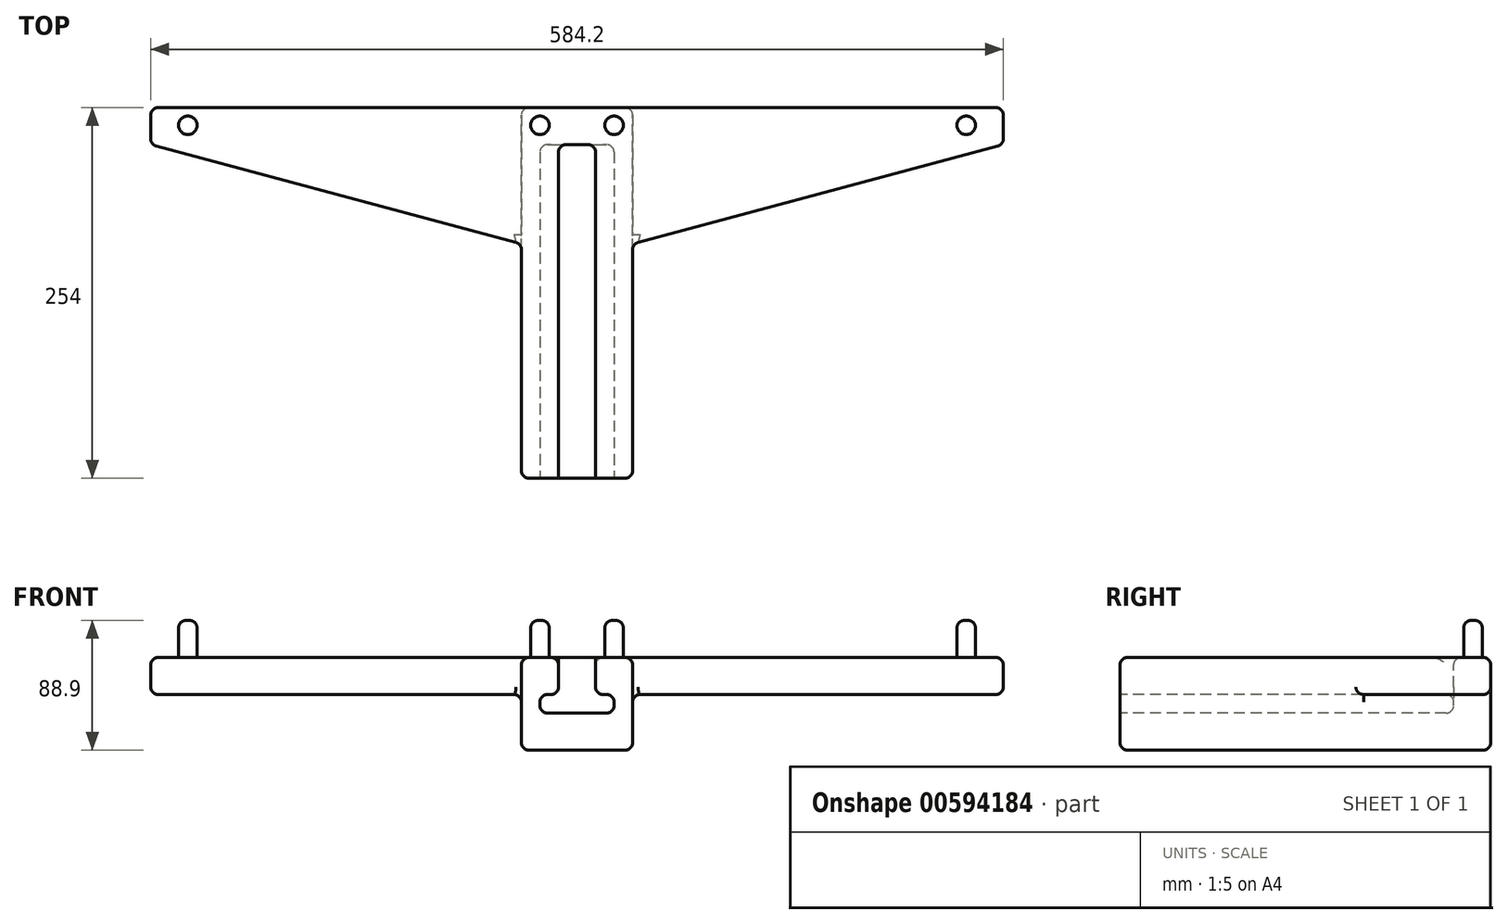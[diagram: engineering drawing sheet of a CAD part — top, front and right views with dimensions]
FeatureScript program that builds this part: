
annotation { "Feature Type Name" : "Feature", "Feature Type Description" : "" }
export const myFeature = defineFeature(function(context is Context, id is Id, definition is map)
    precondition{}
    {
        {
            var Q0;
            Q0=qCreatedBy(makeId("Front.planeOp"),FACE);
            var sketch = newSketch(context, id + "F0", { "sketchPlane" : qUnion([Q0])});
            skLineSegment(sketch, "E0.bottom", {"start": v(-38.93, 38.6) * mm, "end": v(37.27, 38.6) * mm});
            skLineSegment(sketch, "E0.top", {"start": v(-38.93, -24.9) * mm, "end": v(37.27, -24.9) * mm});
            skLineSegment(sketch, "E0.left", {"start": v(-38.93, 38.6) * mm, "end": v(-38.93, -24.9) * mm});
            skLineSegment(sketch, "E0.right", {"start": v(37.27, 38.6) * mm, "end": v(37.27, -24.9) * mm});
            skSolve(sketch);
        }
        {
            var Q0;
            Q0=makeQuery(id+"F0.imprint","IMPRINT",FACE,{"disambiguationData":[TD([[makeQuery(id+"F0.imprint","IMPRINT",EDGE,{"derivedFrom":sQuery(id+"F0.wireOp",EDGE,"E0.bottom")}),-1.0]])]});
            extrude(context, id + "F1", {"entities" : qUnion([Q0]), "endBound" : BoundingType.SYMMETRIC, "depth" : 254 * mm, "offsetDistance" : 25.4 * mm});
        }
        {
            var Q0;
            Q0=makeQuery(id+"F1.opExtrude","CAP_FACE",FACE,{"disambiguationData":[OSD([sQuery(id+"F0.wireOp",EDGE,"E0.bottom"),sQuery(id+"F0.wireOp",EDGE,"E0.top"),sQuery(id+"F0.wireOp",EDGE,"E0.left"),sQuery(id+"F0.wireOp",EDGE,"E0.right")])],"isStart":false});
            var sketch = newSketch(context, id + "F2", { "sketchPlane" : qUnion([Q0])});
            skLineSegment(sketch, "E1", {"start": v(-38.93, 38.6) * mm, "end": v(-13.53, 38.6) * mm, "construction": true});
            skLineSegment(sketch, "E2", {"start": v(37.27, 38.6) * mm, "end": v(11.87, 38.6) * mm, "construction": true});
            skLineSegment(sketch, "E3", {"start": v(-13.53, 38.6) * mm, "end": v(-13.53, 13.2) * mm});
            skLineSegment(sketch, "E4", {"start": v(-13.53, 13.2) * mm, "end": v(-26.23, 13.2) * mm});
            skLineSegment(sketch, "E5", {"start": v(-26.23, 13.2) * mm, "end": v(-26.23, 0.5) * mm});
            skLineSegment(sketch, "E6", {"start": v(-26.23, 0.5) * mm, "end": v(24.57, 0.5) * mm});
            skLineSegment(sketch, "E7", {"start": v(24.57, 0.5) * mm, "end": v(24.57, 13.2) * mm});
            skLineSegment(sketch, "E8", {"start": v(24.57, 13.2) * mm, "end": v(11.87, 13.2) * mm});
            skLineSegment(sketch, "E9", {"start": v(11.87, 13.2) * mm, "end": v(11.87, 38.6) * mm});
            skLineSegment(sketch, "E10", {"start": v(-13.53, 38.6) * mm, "end": v(11.87, 38.6) * mm});
            skSolve(sketch);
        }
        {
            var Q0;
            Q0 = qSketchRegion(id + "F2", true);
            extrude(context, id + "F3", {"entities" : qUnion([Q0]), "operationType" : NewBodyOperationType.REMOVE, "oppositeDirection" : true, "depth" : 228.6 * mm, "offsetDistance" : 25.4 * mm});
        }
        {
            var Q0;
            Q0=makeQuery(id+"F1.opExtrude","SWEPT_FACE",FACE,{"disambiguationData":[OSD([sQuery(id+"F0.wireOp",EDGE,"E0.bottom")])]});
            var sketch = newSketch(context, id + "F4", { "sketchPlane" : qUnion([Q0])});
            skLineSegment(sketch, "E11", {"start": v(-38.93, 114.88) * mm, "end": v(-26.23, 114.88) * mm, "construction": true});
            skLineSegment(sketch, "E12", {"start": v(37.27, 114.88) * mm, "end": v(24.57, 114.88) * mm, "construction": true});
            skCircle(sketch, "E13", {"center": v(-26.23, 114.88) * mm, "radius": 6.35 * mm});
            skCircle(sketch, "E14", {"center": v(24.57, 114.88) * mm, "radius": 6.35 * mm});
            skSolve(sketch);
        }
        {
            var Q0;
            Q0 = qSketchRegion(id + "F4", true);
            extrude(context, id + "F5", {"entities" : qUnion([Q0]), "operationType" : NewBodyOperationType.ADD, "depth" : 25.4 * mm, "offsetDistance" : 25.4 * mm});
        }
        {
            var Q0;
            Q0=makeQuery(id+"F1.opExtrude","SWEPT_FACE",FACE,{"disambiguationData":[OSD([sQuery(id+"F0.wireOp",EDGE,"E0.right")])]});
            var sketch = newSketch(context, id + "F6", { "sketchPlane" : qUnion([Q0])});
            skLineSegment(sketch, "E15.bottom", {"start": v(127, 38.6) * mm, "end": v(25.4, 38.6) * mm});
            skLineSegment(sketch, "E15.top", {"start": v(127, 13.2) * mm, "end": v(25.4, 13.2) * mm});
            skLineSegment(sketch, "E15.left", {"start": v(127, 38.6) * mm, "end": v(127, 13.2) * mm});
            skLineSegment(sketch, "E15.right", {"start": v(25.4, 38.6) * mm, "end": v(25.4, 13.2) * mm});
            skSolve(sketch);
        }
        {
            var Q0;
            Q0 = qSketchRegion(id + "F6", true);
            extrude(context, id + "F7", {"entities" : qUnion([Q0]), "operationType" : NewBodyOperationType.ADD, "depth" : 254 * mm, "offsetDistance" : 25.4 * mm});
        }
        {
            var Q0;
            Q0=makeQuery(id+"F7.opExtrude","CAP_EDGE",EDGE,{"disambiguationData":[OSD([sQuery(id+"F6.wireOp",EDGE,"E15.right")])],"isStart":false});
            chamfer(context, id + "F8", {"entities" : qUnion([Q0]), "chamferType" : ChamferType.OFFSET_ANGLE, "width" : 76.2 * mm, "oppositeDirection" : false, "angle" : 75 * degree, "tangentPropagation" : true});
        }
        {
            var Q0;
            Q0=makeQuery(id+"F1.opExtrude","SWEPT_FACE",FACE,{"disambiguationData":[OSD([sQuery(id+"F0.wireOp",EDGE,"E0.left")])]});
            var sketch = newSketch(context, id + "F9", { "sketchPlane" : qUnion([Q0])});
            skLineSegment(sketch, "E16.bottom", {"start": v(-127, 38.6) * mm, "end": v(-25.4, 38.6) * mm});
            skLineSegment(sketch, "E16.top", {"start": v(-127, 13.2) * mm, "end": v(-25.4, 13.2) * mm});
            skLineSegment(sketch, "E16.left", {"start": v(-127, 38.6) * mm, "end": v(-127, 13.2) * mm});
            skLineSegment(sketch, "E16.right", {"start": v(-25.4, 38.6) * mm, "end": v(-25.4, 13.2) * mm});
            skSolve(sketch);
        }
        {
            var Q0;
            Q0=makeQuery(id+"F9.imprint","IMPRINT",FACE,{"disambiguationData":[TD([[makeQuery(id+"F9.imprint","IMPRINT",EDGE,{"derivedFrom":sQuery(id+"F9.wireOp",EDGE,"E16.bottom")}),1.0]])]});
            extrude(context, id + "F10", {"entities" : qUnion([Q0]), "operationType" : NewBodyOperationType.ADD, "depth" : 254 * mm, "offsetDistance" : 25.4 * mm});
        }
        {
            var Q0;
            Q0=makeQuery(id+"F10.opExtrude","CAP_EDGE",EDGE,{"disambiguationData":[OSD([sQuery(id+"F9.wireOp",EDGE,"E16.right")])],"isStart":false});
            chamfer(context, id + "F11", {"entities" : qUnion([Q0]), "chamferType" : ChamferType.OFFSET_ANGLE, "width" : 76.2 * mm, "oppositeDirection" : true, "angle" : 75 * degree, "tangentPropagation" : true});
        }
        {
            var Q0;
            Q0=makeQuery(id+"F7.opExtrude","SWEPT_EDGE",EDGE,{"disambiguationData":[OSD([sQuery(id+"F0.wireOp",EDGE,"E0.right"),sQuery(id+"F6.wireOp",EDGE,"E15.top"),sQuery(id+"F6.wireOp",EDGE,"E15.left")])]});
            var Q1;
            Q1=makeQuery(id+"F10.opExtrude","SWEPT_EDGE",EDGE,{"disambiguationData":[OSD([sQuery(id+"F0.wireOp",EDGE,"E0.left"),sQuery(id+"F9.wireOp",EDGE,"E16.top"),sQuery(id+"F9.wireOp",EDGE,"E16.left")])]});
            var Q2;
            Q2=makeQuery(id+"F1.opExtrude","CAP_EDGE",EDGE,{"disambiguationData":[OSD([sQuery(id+"F0.wireOp",EDGE,"E0.right")])],"isStart":true});
            var Q3;
            Q3=makeQuery(id+"F1.opExtrude","CAP_EDGE",EDGE,{"disambiguationData":[OSD([sQuery(id+"F0.wireOp",EDGE,"E0.left")])],"isStart":true});
            var Q4;
            Q4=makeQuery(id+"F1.opExtrude","SWEPT_EDGE",EDGE,{"disambiguationData":[OSD([sQuery(id+"F0.wireOp",EDGE,"E0.top"),sQuery(id+"F0.wireOp",EDGE,"E0.left")])]});
            var Q5;
            Q5=makeQuery(id+"F1.opExtrude","CAP_EDGE",EDGE,{"disambiguationData":[OSD([sQuery(id+"F0.wireOp",EDGE,"E0.top")])],"isStart":true});
            var Q6;
            Q6=makeQuery(id+"F1.opExtrude","SWEPT_EDGE",EDGE,{"disambiguationData":[OSD([sQuery(id+"F0.wireOp",EDGE,"E0.top"),sQuery(id+"F0.wireOp",EDGE,"E0.right")])]});
            var Q7;
            Q7=makeQuery(id+"F1.opExtrude","CAP_EDGE",EDGE,{"disambiguationData":[OSD([sQuery(id+"F0.wireOp",EDGE,"E0.top")])],"isStart":false});
            var Q8;
            Q8=makeQuery(id+"F1.opExtrude","SWEPT_EDGE",EDGE,{"disambiguationData":[OSD([sQuery(id+"F0.wireOp",EDGE,"E0.bottom"),sQuery(id+"F0.wireOp",EDGE,"E0.right")])]});
            var Q9;
            Q9=makeQuery(id+"F3.boolean.opBoolean","COPY",EDGE,{"derivedFrom":makeQuery(id+"F3.opExtrude","SWEPT_EDGE",EDGE,{"disambiguationData":[OSD([sQuery(id+"F0.wireOp",EDGE,"E0.bottom"),sQuery(id+"F2.wireOp",EDGE,"E3"),sQuery(id+"F2.wireOp",EDGE,"E10")])]})});
            var Q10;
            Q10=makeQuery(id+"F8.opChamfer","BLEND_EDGE",EDGE,{"blendedFrom":[makeQuery(id+"F7.opExtrude","CAP_EDGE",EDGE,{"disambiguationData":[OSD([sQuery(id+"F6.wireOp",EDGE,"E15.right")])],"isStart":false}),makeQuery(id+"F7.boolean.opBoolean","MERGE",FACE,{"derivedFrom":[makeQuery(id+"F1.opExtrude","SWEPT_FACE",FACE,{"disambiguationData":[OSD([sQuery(id+"F0.wireOp",EDGE,"E0.bottom")])]}),makeQuery(id+"F7.opExtrude","SWEPT_FACE",FACE,{"disambiguationData":[OSD([sQuery(id+"F6.wireOp",EDGE,"E15.bottom")])]})]})],"blendedInto":[makeQuery(id+"F7.boolean.opBoolean","MERGE",FACE,{"derivedFrom":[makeQuery(id+"F1.opExtrude","SWEPT_FACE",FACE,{"disambiguationData":[OSD([sQuery(id+"F0.wireOp",EDGE,"E0.bottom")])]}),makeQuery(id+"F7.opExtrude","SWEPT_FACE",FACE,{"disambiguationData":[OSD([sQuery(id+"F6.wireOp",EDGE,"E15.bottom")])]})]})]});
            var Q11;
            Q11=makeQuery(id+"F11.opChamfer","BLEND_EDGE",EDGE,{"blendedFrom":[makeQuery(id+"F10.opExtrude","CAP_EDGE",EDGE,{"disambiguationData":[OSD([sQuery(id+"F9.wireOp",EDGE,"E16.right")])],"isStart":false}),makeQuery(id+"F10.boolean.opBoolean","MERGE",FACE,{"derivedFrom":[makeQuery(id+"F7.boolean.opBoolean","MERGE",FACE,{"derivedFrom":[makeQuery(id+"F1.opExtrude","SWEPT_FACE",FACE,{"disambiguationData":[OSD([sQuery(id+"F0.wireOp",EDGE,"E0.bottom")])]}),makeQuery(id+"F7.opExtrude","SWEPT_FACE",FACE,{"disambiguationData":[OSD([sQuery(id+"F6.wireOp",EDGE,"E15.bottom")])]})]}),makeQuery(id+"F10.opExtrude","SWEPT_FACE",FACE,{"disambiguationData":[OSD([sQuery(id+"F9.wireOp",EDGE,"E16.bottom")])]})]})],"blendedInto":[makeQuery(id+"F10.boolean.opBoolean","MERGE",FACE,{"derivedFrom":[makeQuery(id+"F7.boolean.opBoolean","MERGE",FACE,{"derivedFrom":[makeQuery(id+"F1.opExtrude","SWEPT_FACE",FACE,{"disambiguationData":[OSD([sQuery(id+"F0.wireOp",EDGE,"E0.bottom")])]}),makeQuery(id+"F7.opExtrude","SWEPT_FACE",FACE,{"disambiguationData":[OSD([sQuery(id+"F6.wireOp",EDGE,"E15.bottom")])]})]}),makeQuery(id+"F10.opExtrude","SWEPT_FACE",FACE,{"disambiguationData":[OSD([sQuery(id+"F9.wireOp",EDGE,"E16.bottom")])]})]})]});
            var Q12;
            Q12=makeQuery(id+"F3.boolean.opBoolean","COPY",EDGE,{"derivedFrom":makeQuery(id+"F3.opExtrude","CAP_EDGE",EDGE,{"disambiguationData":[OSD([sQuery(id+"F2.wireOp",EDGE,"E9")])],"isStart":true})});
            var Q13;
            Q13=makeQuery(id+"F3.boolean.opBoolean","COPY",EDGE,{"derivedFrom":makeQuery(id+"F3.opExtrude","CAP_EDGE",EDGE,{"disambiguationData":[OSD([sQuery(id+"F2.wireOp",EDGE,"E3")])],"isStart":true})});
            var Q14;
            Q14=makeQuery(id+"F3.boolean.opBoolean","COPY",EDGE,{"derivedFrom":makeQuery(id+"F3.opExtrude","CAP_EDGE",EDGE,{"disambiguationData":[OSD([sQuery(id+"F2.wireOp",EDGE,"E6")])],"isStart":true})});
            var Q15;
            Q15=makeQuery(id+"F3.boolean.opBoolean","COPY",EDGE,{"derivedFrom":makeQuery(id+"F3.opExtrude","SWEPT_EDGE",EDGE,{"disambiguationData":[OSD([sQuery(id+"F2.wireOp",EDGE,"E6"),sQuery(id+"F2.wireOp",EDGE,"E7")])]})});
            var Q16;
            Q16=makeQuery(id+"F3.boolean.opBoolean","COPY",EDGE,{"derivedFrom":makeQuery(id+"F3.opExtrude","SWEPT_EDGE",EDGE,{"disambiguationData":[OSD([sQuery(id+"F2.wireOp",EDGE,"E8"),sQuery(id+"F2.wireOp",EDGE,"E9")])]})});
            var Q17;
            Q17=makeQuery(id+"F3.boolean.opBoolean","COPY",EDGE,{"derivedFrom":makeQuery(id+"F3.opExtrude","SWEPT_EDGE",EDGE,{"disambiguationData":[OSD([sQuery(id+"F2.wireOp",EDGE,"E3"),sQuery(id+"F2.wireOp",EDGE,"E4")])]})});
            var Q18;
            Q18=makeQuery(id+"F1.opExtrude","CAP_EDGE",EDGE,{"disambiguationData":[OSD([sQuery(id+"F0.wireOp",EDGE,"E0.right")])],"isStart":false});
            var Q19;
            Q19=makeQuery(id+"F3.boolean.opBoolean","COPY",EDGE,{"derivedFrom":makeQuery(id+"F3.opExtrude","SWEPT_EDGE",EDGE,{"disambiguationData":[OSD([sQuery(id+"F2.wireOp",EDGE,"E4"),sQuery(id+"F2.wireOp",EDGE,"E5")])]})});
            var Q20;
            Q20=makeQuery(id+"F3.boolean.opBoolean","COPY",EDGE,{"derivedFrom":makeQuery(id+"F3.opExtrude","SWEPT_EDGE",EDGE,{"disambiguationData":[OSD([sQuery(id+"F2.wireOp",EDGE,"E5"),sQuery(id+"F2.wireOp",EDGE,"E6")])]})});
            var Q21;
            Q21=makeQuery(id+"F3.boolean.opBoolean","COPY",EDGE,{"derivedFrom":makeQuery(id+"F3.opExtrude","CAP_EDGE",EDGE,{"disambiguationData":[OSD([sQuery(id+"F2.wireOp",EDGE,"E8")])],"isStart":true})});
            var Q22;
            Q22=makeQuery(id+"F1.opExtrude","SWEPT_FACE",FACE,{"disambiguationData":[OSD([sQuery(id+"F0.wireOp",EDGE,"E0.left")])]});
            var Q23;
            Q23=makeQuery(id+"F1.opExtrude","SWEPT_FACE",FACE,{"disambiguationData":[OSD([sQuery(id+"F0.wireOp",EDGE,"E0.right")])]});
            var Q24;
            Q24=makeQuery(id+"F3.boolean.opBoolean","COPY",EDGE,{"derivedFrom":makeQuery(id+"F3.opExtrude","SWEPT_EDGE",EDGE,{"disambiguationData":[OSD([sQuery(id+"F0.wireOp",EDGE,"E0.bottom"),sQuery(id+"F2.wireOp",EDGE,"E9"),sQuery(id+"F2.wireOp",EDGE,"E10")])]})});
            var Q25;
            {var subQ0=sQuery(id+"F0.wireOp",EDGE,"E0.bottom");var subQ1=sQuery(id+"F0.wireOp",EDGE,"E0.right");Q25=makeQuery(id+"F3.boolean.opBoolean","SPLIT",EDGE,{"disambiguationData":[TD([makeQuery(id+"F1.opExtrude","SWEPT_FACE",FACE,{"disambiguationData":[OSD([subQ1])]})])],"derivedFrom":makeQuery(id+"F1.opExtrude","CAP_EDGE",EDGE,{"disambiguationData":[OSD([subQ0])],"isStart":false})});}
            var Q26;
            {var subQ0=sQuery(id+"F0.wireOp",EDGE,"E0.bottom");var subQ1=sQuery(id+"F0.wireOp",EDGE,"E0.left");Q26=makeQuery(id+"F3.boolean.opBoolean","SPLIT",EDGE,{"disambiguationData":[TD([makeQuery(id+"F1.opExtrude","SWEPT_FACE",FACE,{"disambiguationData":[OSD([subQ1])]})])],"derivedFrom":makeQuery(id+"F1.opExtrude","CAP_EDGE",EDGE,{"disambiguationData":[OSD([subQ0])],"isStart":false})});}
            var Q27;
            Q27=makeQuery(id+"F10.boolean.opBoolean","MERGE",EDGE,{"derivedFrom":[makeQuery(id+"F7.boolean.opBoolean","MERGE",EDGE,{"derivedFrom":[makeQuery(id+"F1.opExtrude","CAP_EDGE",EDGE,{"disambiguationData":[OSD([sQuery(id+"F0.wireOp",EDGE,"E0.bottom")])],"isStart":true}),makeQuery(id+"F7.opExtrude","SWEPT_EDGE",EDGE,{"disambiguationData":[OSD([sQuery(id+"F6.wireOp",EDGE,"E15.bottom"),sQuery(id+"F6.wireOp",EDGE,"E15.left")])]})]}),makeQuery(id+"F10.opExtrude","SWEPT_EDGE",EDGE,{"disambiguationData":[OSD([sQuery(id+"F9.wireOp",EDGE,"E16.bottom"),sQuery(id+"F9.wireOp",EDGE,"E16.left")])]})]});
            var Q28;
            Q28=makeQuery(id+"F3.boolean.opBoolean","COPY",EDGE,{"derivedFrom":makeQuery(id+"F3.opExtrude","SWEPT_EDGE",EDGE,{"disambiguationData":[OSD([sQuery(id+"F2.wireOp",EDGE,"E7"),sQuery(id+"F2.wireOp",EDGE,"E8")])]})});
            var Q29;
            Q29=makeQuery(id+"F3.boolean.opBoolean","COPY",FACE,{"derivedFrom":makeQuery(id+"F3.opExtrude","CAP_FACE",FACE,{"disambiguationData":[OSD([sQuery(id+"F2.wireOp",EDGE,"E3"),sQuery(id+"F2.wireOp",EDGE,"E4"),sQuery(id+"F2.wireOp",EDGE,"E5"),sQuery(id+"F2.wireOp",EDGE,"E6"),sQuery(id+"F2.wireOp",EDGE,"E7"),sQuery(id+"F2.wireOp",EDGE,"E8"),sQuery(id+"F2.wireOp",EDGE,"E9"),sQuery(id+"F2.wireOp",EDGE,"E10")])],"isStart":false})});
            var Q30;
            Q30=makeQuery(id+"F5.opExtrude","CAP_EDGE",EDGE,{"disambiguationData":[OSD([sQuery(id+"F4.wireOp",EDGE,"E14")])],"isStart":false});
            var Q31;
            Q31=makeQuery(id+"F5.opExtrude","CAP_EDGE",EDGE,{"disambiguationData":[OSD([sQuery(id+"F4.wireOp",EDGE,"E13")])],"isStart":false});
            var Q32;
            Q32=makeQuery(id+"F11.opChamfer","BLEND_EDGE",EDGE,{"blendedFrom":[makeQuery(id+"F10.opExtrude","CAP_EDGE",EDGE,{"disambiguationData":[OSD([sQuery(id+"F9.wireOp",EDGE,"E16.right")])],"isStart":false}),makeQuery(id+"F10.opExtrude","SWEPT_FACE",FACE,{"disambiguationData":[OSD([sQuery(id+"F9.wireOp",EDGE,"E16.top")])]})],"blendedInto":[makeQuery(id+"F10.opExtrude","SWEPT_FACE",FACE,{"disambiguationData":[OSD([sQuery(id+"F9.wireOp",EDGE,"E16.top")])]})]});
            var Q33;
            Q33=makeQuery(id+"F10.opExtrude","CAP_FACE",FACE,{"disambiguationData":[OSD([sQuery(id+"F9.wireOp",EDGE,"E16.bottom"),sQuery(id+"F9.wireOp",EDGE,"E16.top"),sQuery(id+"F9.wireOp",EDGE,"E16.left"),sQuery(id+"F9.wireOp",EDGE,"E16.right")])],"isStart":false});
            var Q34;
            Q34=makeQuery(id+"F7.opExtrude","CAP_FACE",FACE,{"disambiguationData":[OSD([sQuery(id+"F6.wireOp",EDGE,"E15.bottom"),sQuery(id+"F6.wireOp",EDGE,"E15.top"),sQuery(id+"F6.wireOp",EDGE,"E15.left"),sQuery(id+"F6.wireOp",EDGE,"E15.right")])],"isStart":false});
            var Q35;
            Q35=makeQuery(id+"F7.opExtrude","SWEPT_FACE",FACE,{"disambiguationData":[OSD([sQuery(id+"F6.wireOp",EDGE,"E15.top")])]});
            fillet(context, id + "F12", {"entities" : qUnion([Q0, Q1, Q2, Q3, Q4, Q5, Q6, Q7, Q8, Q9, Q10, Q11, Q12, Q13, Q14, Q15, Q16, Q17, Q18, Q19, Q20, Q21, Q22, Q23, Q24, Q25, Q26, Q27, Q28, Q29, Q30, Q31, Q32, Q33, Q34, Q35]), "radius" : 5.08 * mm, "tangentPropagation" : true, "allowEdgeOverflow" : false});
        }
        {
            var Q0;
            Q0=makeQuery(id+"F10.boolean.opBoolean","MERGE",FACE,{"derivedFrom":[makeQuery(id+"F7.boolean.opBoolean","MERGE",FACE,{"derivedFrom":[makeQuery(id+"F1.opExtrude","SWEPT_FACE",FACE,{"disambiguationData":[OSD([sQuery(id+"F0.wireOp",EDGE,"E0.bottom")])]}),makeQuery(id+"F7.opExtrude","SWEPT_FACE",FACE,{"disambiguationData":[OSD([sQuery(id+"F6.wireOp",EDGE,"E15.bottom")])]})]}),makeQuery(id+"F10.opExtrude","SWEPT_FACE",FACE,{"disambiguationData":[OSD([sQuery(id+"F9.wireOp",EDGE,"E16.bottom")])]})]});
            var sketch = newSketch(context, id + "F13", { "sketchPlane" : qUnion([Q0])});
            skLineSegment(sketch, "E17", {"start": v(24.57, 114.88) * mm, "end": v(265.87, 114.88) * mm, "construction": true});
            skLineSegment(sketch, "E18", {"start": v(-26.23, 114.88) * mm, "end": v(-267.53, 114.88) * mm, "construction": true});
            skCircle(sketch, "E19", {"center": v(-267.53, 114.88) * mm, "radius": 6.35 * mm});
            skCircle(sketch, "E20", {"center": v(265.87, 114.88) * mm, "radius": 6.35 * mm});
            skSolve(sketch);
        }
        {
            var Q0;
            Q0 = qSketchRegion(id + "F13", true);
            extrude(context, id + "F14", {"entities" : qUnion([Q0]), "operationType" : NewBodyOperationType.ADD, "depth" : 25.4 * mm, "offsetDistance" : 25.4 * mm});
        }
        {
            var Q0;
            Q0=makeQuery(id+"F14.opExtrude","CAP_EDGE",EDGE,{"disambiguationData":[OSD([sQuery(id+"F13.wireOp",EDGE,"E19")])],"isStart":false});
            var Q1;
            Q1=makeQuery(id+"F14.opExtrude","CAP_EDGE",EDGE,{"disambiguationData":[OSD([sQuery(id+"F13.wireOp",EDGE,"E20")])],"isStart":false});
            fillet(context, id + "F15", {"entities" : qUnion([Q0, Q1]), "radius" : 5.08 * mm, "tangentPropagation" : true, "allowEdgeOverflow" : false});
        }
    });
